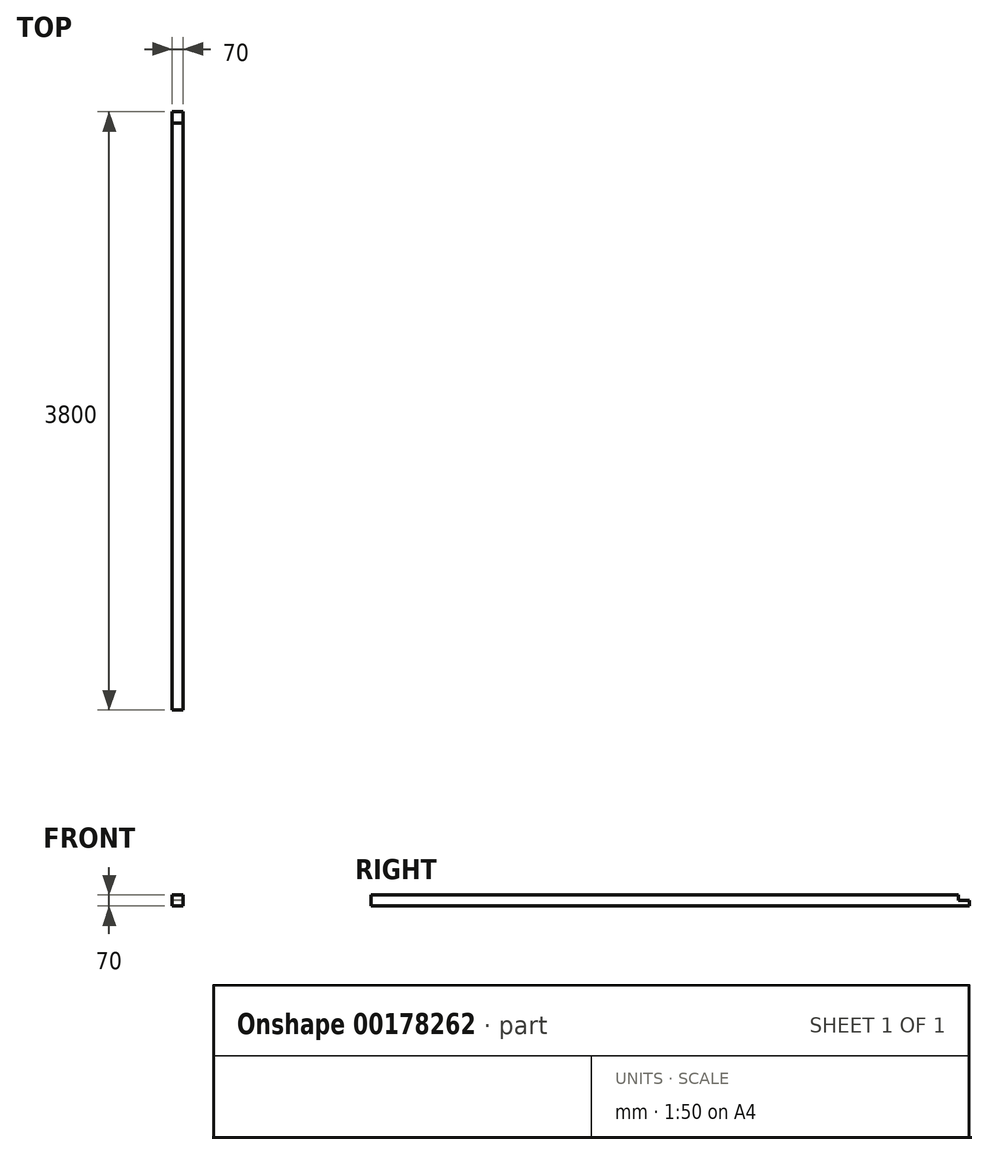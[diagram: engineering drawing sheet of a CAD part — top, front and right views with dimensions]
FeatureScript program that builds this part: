
annotation { "Feature Type Name" : "Feature", "Feature Type Description" : "" }
export const myFeature = defineFeature(function(context is Context, id is Id, definition is map)
    precondition{}
    {
        {
            var Q0;
            Q0=qCreatedBy(makeId("Front.planeOp"),FACE);
            var sketch = newSketch(context, id + "F0", { "sketchPlane" : qUnion([Q0])});
            skLineSegment(sketch, "E0.bottom", {"start": v(35, -35) * mm, "end": v(-35, -35) * mm});
            skLineSegment(sketch, "E0.top", {"start": v(35, 35) * mm, "end": v(-35, 35) * mm});
            skLineSegment(sketch, "E0.left", {"start": v(35, -35) * mm, "end": v(35, 35) * mm});
            skLineSegment(sketch, "E0.right", {"start": v(-35, -35) * mm, "end": v(-35, 35) * mm});
            skPoint(sketch, "E0.middle", {"position": v(0, 0) * mm});
            skSolve(sketch);
        }
        {
            var Q0;
            Q0 = qSketchRegion(id + "F0", true);
            extrude(context, id + "F1", {"entities" : qUnion([Q0]), "depth" : 3800 * mm});
        }
        {
            var Q0;
            Q0=makeQuery(id+"F1.opExtrude","SWEPT_FACE",FACE,{"disambiguationData":[OSD([sQuery(id+"F0.wireOp",EDGE,"E0.top")])]});
            var sketch = newSketch(context, id + "F2", { "sketchPlane" : qUnion([Q0])});
            skLineSegment(sketch, "E1.bottom", {"start": v(35, 0) * mm, "end": v(-35, 0) * mm});
            skLineSegment(sketch, "E1.top", {"start": v(35, -70) * mm, "end": v(-35, -70) * mm});
            skLineSegment(sketch, "E1.left", {"start": v(35, 0) * mm, "end": v(35, -70) * mm});
            skLineSegment(sketch, "E1.right", {"start": v(-35, 0) * mm, "end": v(-35, -70) * mm});
            skSolve(sketch);
        }
        {
            var Q0;
            Q0=makeQuery(id+"F2.imprint","IMPRINT",FACE,{"disambiguationData":[TD([[makeQuery(id+"F2.imprint","IMPRINT",EDGE,{"derivedFrom":sQuery(id+"F2.wireOp",EDGE,"E1.bottom")}),1.0]])]});
            extrude(context, id + "F3", {"entities" : qUnion([Q0]), "operationType" : NewBodyOperationType.REMOVE, "oppositeDirection" : true, "depth" : 35 * mm});
        }
    });
